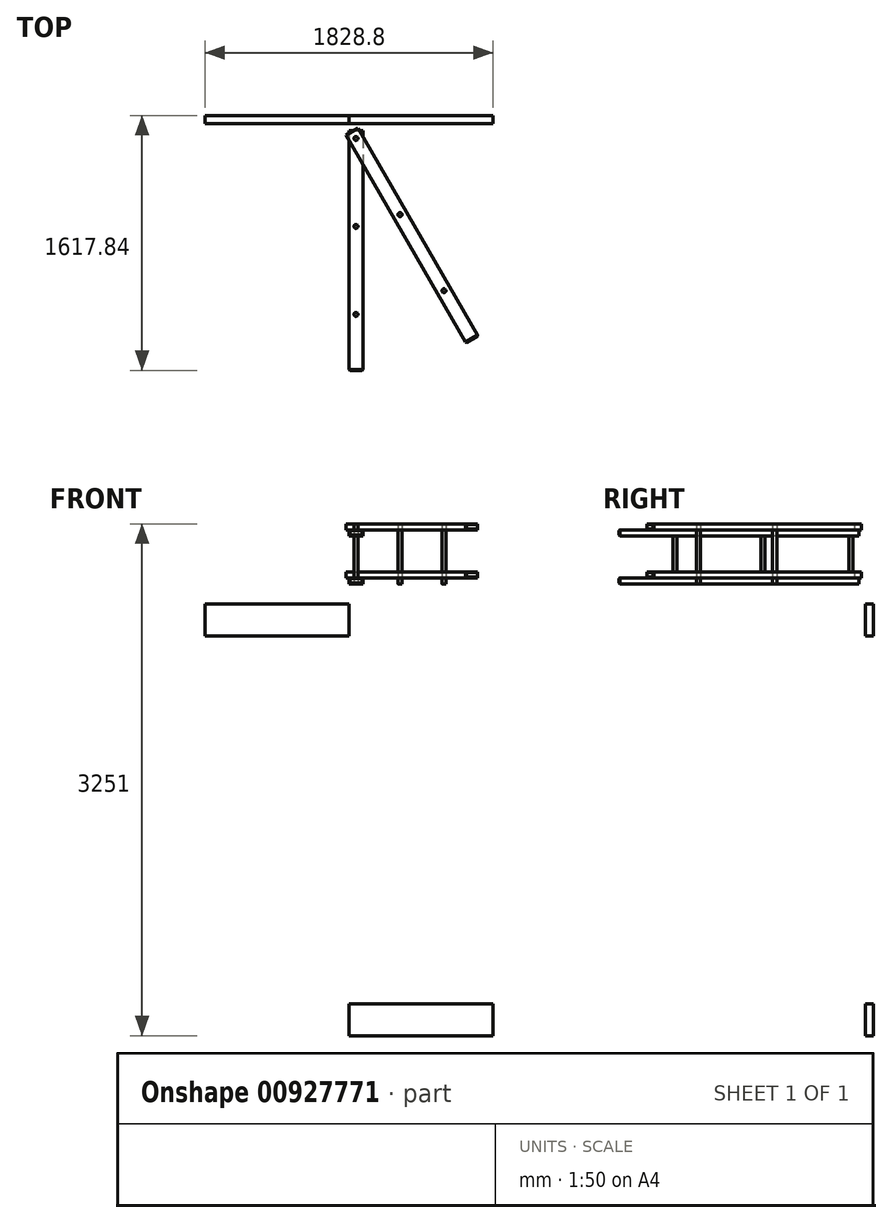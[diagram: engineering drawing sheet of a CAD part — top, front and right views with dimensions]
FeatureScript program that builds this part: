
annotation { "Feature Type Name" : "Feature", "Feature Type Description" : "" }
export const myFeature = defineFeature(function(context is Context, id is Id, definition is map)
    precondition{}
    {
        {
            var Q0;
            Q0=qCreatedBy(makeId("Front.planeOp"),FACE);
            var sketch = newSketch(context, id + "F0", { "sketchPlane" : qUnion([Q0])});
            skLineSegment(sketch, "E0.bottom", {"start": v(-253.64, -44.04) * mm, "end": v(-164.74, -44.04) * mm});
            skLineSegment(sketch, "E0.top", {"start": v(-253.64, -82.14) * mm, "end": v(-164.74, -82.14) * mm});
            skLineSegment(sketch, "E0.left", {"start": v(-253.64, -44.04) * mm, "end": v(-253.64, -82.14) * mm});
            skLineSegment(sketch, "E0.right", {"start": v(-164.74, -44.04) * mm, "end": v(-164.74, -82.14) * mm});
            skPoint(sketch, "E1.firstSnap0", {"position": v(-209.2, -44.04) * mm});
            skSolve(sketch);
        }
        {
            var Q0;
            Q0 = qSketchRegion(id + "F0", true);
            extrude(context, id + "F1", {"entities" : qUnion([Q0]), "oppositeDirection" : true, "depth" : 1524 * mm, "offsetDistance" : 25.4 * mm});
        }
        {
            var Q0;
            Q0=makeQuery(id+"F1.opExtrude","SWEPT_BODY",BODY,{"disambiguationData":[OSD([sQuery(id+"F0.wireOp",EDGE,"E0.bottom"),sQuery(id+"F0.wireOp",EDGE,"E0.top"),sQuery(id+"F0.wireOp",EDGE,"E0.left"),sQuery(id+"F0.wireOp",EDGE,"E0.right")])]});
            var Q1;
            Q1=qCreatedBy(makeId("Top.planeOp"),FACE);
            transform(context, id + "F2", {"entities" : qUnion([Q0]), "transformType" : TransformType.TRANSLATION_DISTANCE, "transformDirection" : qUnion([Q1]), "distance" : 304.8 * mm, "makeCopy" : true});
        }
        {
            var Q0;
            Q0=makeQuery(id+"FAnmGfrz1Be9Owt_1.opPattern","COPY",FACE,{"derivedFrom":makeQuery(id+"F2.opPattern","COPY",FACE,{"derivedFrom":makeQuery(id+"F1.opExtrude","CAP_FACE",FACE,{"disambiguationData":[OSD([sQuery(id+"F0.wireOp",EDGE,"E0.bottom"),sQuery(id+"F0.wireOp",EDGE,"E0.top"),sQuery(id+"F0.wireOp",EDGE,"E0.left"),sQuery(id+"F0.wireOp",EDGE,"E0.right")])],"isStart":true}),"instanceName":"1"}),"instanceName":"1"});
            var Q1;
            Q1=makeQuery(id+"FAnmGfrz1Be9Owt_1.opPattern","COPY",FACE,{"derivedFrom":makeQuery(id+"F1.opExtrude","CAP_FACE",FACE,{"disambiguationData":[OSD([sQuery(id+"F0.wireOp",EDGE,"E0.bottom"),sQuery(id+"F0.wireOp",EDGE,"E0.top"),sQuery(id+"F0.wireOp",EDGE,"E0.left"),sQuery(id+"F0.wireOp",EDGE,"E0.right")])],"isStart":true}),"instanceName":"1"});
            var Q2;
            Q2=makeQuery(id+"F1.opExtrude","CAP_FACE",FACE,{"disambiguationData":[OSD([sQuery(id+"F0.wireOp",EDGE,"E0.bottom"),sQuery(id+"F0.wireOp",EDGE,"E0.top"),sQuery(id+"F0.wireOp",EDGE,"E0.left"),sQuery(id+"F0.wireOp",EDGE,"E0.right")])],"isStart":true});
            var Q3;
            Q3=makeQuery(id+"F2.opPattern","COPY",FACE,{"derivedFrom":makeQuery(id+"F1.opExtrude","CAP_FACE",FACE,{"disambiguationData":[OSD([sQuery(id+"F0.wireOp",EDGE,"E0.bottom"),sQuery(id+"F0.wireOp",EDGE,"E0.top"),sQuery(id+"F0.wireOp",EDGE,"E0.left"),sQuery(id+"F0.wireOp",EDGE,"E0.right")])],"isStart":true}),"instanceName":"1"});
            chamfer(context, id + "F3", {"entities" : qUnion([Q0, Q1, Q2, Q3]), "width" : 5.08 * mm, "tangentPropagation" : true});
        }
        {
            var Q0;
            Q0=makeQuery(id+"F1.opExtrude","SWEPT_FACE",FACE,{"disambiguationData":[OSD([sQuery(id+"F0.wireOp",EDGE,"E0.top")])]});
            var sketch = newSketch(context, id + "F4", { "sketchPlane" : qUnion([Q0])});
            skCircle(sketch, "E2", {"center": v(-209.2, -1473.2) * mm, "radius": 12.7 * mm});
            skSolve(sketch);
        }
        {
            var Q0;
            Q0=makeQuery(id+"F4.imprint","IMPRINT",FACE,{"disambiguationData":[TD([[makeQuery(id+"F4.imprint","IMPRINT",EDGE,{"derivedFrom":sQuery(id+"F4.wireOp",EDGE,"E2")}),1.0]])]});
            extrude(context, id + "F5", {"entities" : qUnion([Q0]), "oppositeDirection" : true, "depth" : 381 * mm, "offsetDistance" : 25.4 * mm});
        }
        {
            var Q0;
            Q0=makeQuery(id+"F1.opExtrude","SWEPT_BODY",BODY,{"disambiguationData":[OSD([sQuery(id+"F0.wireOp",EDGE,"E0.bottom"),sQuery(id+"F0.wireOp",EDGE,"E0.top"),sQuery(id+"F0.wireOp",EDGE,"E0.left"),sQuery(id+"F0.wireOp",EDGE,"E0.right")])]});
            var Q1;
            Q1=makeQuery(id+"F2.opPattern","COPY",BODY,{"derivedFrom":makeQuery(id+"F1.opExtrude","SWEPT_BODY",BODY,{"disambiguationData":[OSD([sQuery(id+"F0.wireOp",EDGE,"E0.bottom"),sQuery(id+"F0.wireOp",EDGE,"E0.top"),sQuery(id+"F0.wireOp",EDGE,"E0.left"),sQuery(id+"F0.wireOp",EDGE,"E0.right")])]}),"instanceName":"1"});
            var Q2;
            Q2=makeQuery(id+"F5.opExtrude","SWEPT_FACE",FACE,{"disambiguationData":[OSD([sQuery(id+"F4.wireOp",EDGE,"E2")])]});
            transform(context, id + "F6", {"entities" : qUnion([Q0, Q1]), "transformType" : TransformType.ROTATION, "transformAxis" : qUnion([Q2]), "angle" : 30 * degree, "oppositeDirection" : true, "makeCopy" : true});
        }
        {
            var Q0;
            Q0=makeQuery(id+"F6.opPattern","COPY",BODY,{"derivedFrom":makeQuery(id+"F2.opPattern","COPY",BODY,{"derivedFrom":makeQuery(id+"F1.opExtrude","SWEPT_BODY",BODY,{"disambiguationData":[OSD([sQuery(id+"F0.wireOp",EDGE,"E0.bottom"),sQuery(id+"F0.wireOp",EDGE,"E0.top"),sQuery(id+"F0.wireOp",EDGE,"E0.left"),sQuery(id+"F0.wireOp",EDGE,"E0.right")])]}),"instanceName":"1"}),"instanceName":"1"});
            var Q1;
            Q1=makeQuery(id+"F6.opPattern","COPY",BODY,{"derivedFrom":makeQuery(id+"F1.opExtrude","SWEPT_BODY",BODY,{"disambiguationData":[OSD([sQuery(id+"F0.wireOp",EDGE,"E0.bottom"),sQuery(id+"F0.wireOp",EDGE,"E0.top"),sQuery(id+"F0.wireOp",EDGE,"E0.left"),sQuery(id+"F0.wireOp",EDGE,"E0.right")])]}),"instanceName":"1"});
            var Q2;
            Q2=makeQuery(id+"F2.opPattern","COPY",FACE,{"derivedFrom":makeQuery(id+"F1.opExtrude","SWEPT_FACE",FACE,{"disambiguationData":[OSD([sQuery(id+"F0.wireOp",EDGE,"E0.bottom")])]}),"instanceName":"1"});
            transform(context, id + "F7", {"entities" : qUnion([Q0, Q1]), "transformType" : TransformType.TRANSLATION_DISTANCE, "transformDirection" : qUnion([Q2]), "distance" : 38.1 * mm, "makeCopy" : false});
        }
        {
            var Q0;
            Q0=makeQuery(id+"F5.opExtrude","SWEPT_BODY",BODY,{"disambiguationData":[OSD([sQuery(id+"F4.wireOp",EDGE,"E2")])]});
            var Q1;
            Q1=qCreatedBy(makeId("Front.planeOp"),FACE);
            transform(context, id + "F8", {"entities" : qUnion([Q0]), "transformType" : TransformType.TRANSLATION_DISTANCE, "transformDirection" : qUnion([Q1]), "distance" : 558.8 * mm, "makeCopy" : true});
        }
        {
            var Q0;
            Q0=makeQuery(id+"F8.opPattern","COPY",BODY,{"derivedFrom":makeQuery(id+"F5.opExtrude","SWEPT_BODY",BODY,{"disambiguationData":[OSD([sQuery(id+"F4.wireOp",EDGE,"E2")])]}),"instanceName":"1"});
            var Q1;
            Q1=qCreatedBy(makeId("Front.planeOp"),FACE);
            transform(context, id + "F9", {"entities" : qUnion([Q0]), "transformType" : TransformType.TRANSLATION_DISTANCE, "transformDirection" : qUnion([Q1]), "distance" : 558.8 * mm, "makeCopy" : true});
        }
        {
            var Q0;
            Q0=makeQuery(id+"F8.opPattern","COPY",BODY,{"derivedFrom":makeQuery(id+"F5.opExtrude","SWEPT_BODY",BODY,{"disambiguationData":[OSD([sQuery(id+"F4.wireOp",EDGE,"E2")])]}),"instanceName":"1"});
            var Q1;
            Q1=makeQuery(id+"F9.opPattern","COPY",BODY,{"derivedFrom":makeQuery(id+"F8.opPattern","COPY",BODY,{"derivedFrom":makeQuery(id+"F5.opExtrude","SWEPT_BODY",BODY,{"disambiguationData":[OSD([sQuery(id+"F4.wireOp",EDGE,"E2")])]}),"instanceName":"1"}),"instanceName":"1"});
            var Q2;
            Q2=makeQuery(id+"F5.opExtrude","SWEPT_FACE",FACE,{"disambiguationData":[OSD([sQuery(id+"F4.wireOp",EDGE,"E2")])]});
            transform(context, id + "F10", {"entities" : qUnion([Q0, Q1]), "transformType" : TransformType.ROTATION, "transformAxis" : qUnion([Q2]), "angle" : 30 * degree, "oppositeDirection" : true, "makeCopy" : true});
        }
        {
            var Q0;
            Q0=makeQuery(id+"F1.opExtrude","SWEPT_FACE",FACE,{"disambiguationData":[OSD([sQuery(id+"F0.wireOp",EDGE,"E0.left")])]});
            var sketch = newSketch(context, id + "F11", { "sketchPlane" : qUnion([Q0])});
            skLineSegment(sketch, "E3.bottom", {"start": v(-1617.84, -412.14) * mm, "end": v(-1567.04, -412.14) * mm});
            skLineSegment(sketch, "E3.top", {"start": v(-1617.84, -208.94) * mm, "end": v(-1567.04, -208.94) * mm});
            skLineSegment(sketch, "E3.left", {"start": v(-1617.84, -412.14) * mm, "end": v(-1617.84, -208.94) * mm});
            skLineSegment(sketch, "E3.right", {"start": v(-1567.04, -412.14) * mm, "end": v(-1567.04, -208.94) * mm});
            skSolve(sketch);
        }
        {
            var Q0;
            Q0=makeQuery(id+"F11.imprint","IMPRINT",FACE,{"disambiguationData":[TD([[makeQuery(id+"F11.imprint","IMPRINT",EDGE,{"derivedFrom":sQuery(id+"F11.wireOp",EDGE,"E3.bottom")}),1.0]])]});
            extrude(context, id + "F12", {"entities" : qUnion([Q0]), "depth" : 914.4 * mm, "offsetDistance" : 25.4 * mm});
        }
        {
            var Q0;
            Q0=makeQuery(id+"F12.opExtrude","SWEPT_BODY",BODY,{"disambiguationData":[OSD([sQuery(id+"F11.wireOp",EDGE,"E3.bottom"),sQuery(id+"F11.wireOp",EDGE,"E3.top"),sQuery(id+"F11.wireOp",EDGE,"E3.left"),sQuery(id+"F11.wireOp",EDGE,"E3.right")])]});
            var Q1;
            Q1=makeQuery(id+"F12.opExtrude","SWEPT_EDGE",EDGE,{"disambiguationData":[OSD([sQuery(id+"F11.wireOp",EDGE,"E3.bottom"),sQuery(id+"F11.wireOp",EDGE,"E3.right")])]});
            transform(context, id + "F13", {"entities" : qUnion([Q0]), "transformType" : TransformType.TRANSLATION_ENTITY, "oppositeDirectionEntity" : false, "transformLine" : qUnion([Q1]), "makeCopy" : true});
        }
        {
            var Q0;
            Q0=makeQuery(id+"F13.opPattern","COPY",BODY,{"derivedFrom":makeQuery(id+"F12.opExtrude","SWEPT_BODY",BODY,{"disambiguationData":[OSD([sQuery(id+"F11.wireOp",EDGE,"E3.bottom"),sQuery(id+"F11.wireOp",EDGE,"E3.top"),sQuery(id+"F11.wireOp",EDGE,"E3.left"),sQuery(id+"F11.wireOp",EDGE,"E3.right")])]}),"instanceName":"1"});
            var Q1;
            Q1=makeQuery(id+"F6.opPattern","COPY",FACE,{"derivedFrom":makeQuery(id+"F1.opExtrude","SWEPT_FACE",FACE,{"disambiguationData":[OSD([sQuery(id+"F0.wireOp",EDGE,"E0.top")])]}),"instanceName":"1"});
            transform(context, id + "F14", {"entities" : qUnion([Q0]), "transformType" : TransformType.TRANSLATION_DISTANCE, "transformDirection" : qUnion([Q1]), "distance" : 2540 * mm, "makeCopy" : false});
        }
    });
